FCSTD DOCUMENT  (FreeCAD 0.20R29410 (Git))
Label: prancha-editavel-A1-modelo
License: All rights reserved
objects: Sketcher::SketchObject×1
note: 1 computed .brp shape members not serialized (recipe doc carries the construction recipe); baked Part::Feature solids carry a one-line shape summary decoded from their .brp

FEATURE [Sketcher::SketchObject] Sketch
  FullyConstrained = false
  sketch-geometry (12):
    g0: LineSegment StartX=-656.822 StartY=319.687 StartZ=0 EndX=184.178 EndY=319.687 EndZ=0
    g1: LineSegment StartX=184.178 StartY=319.687 StartZ=0 EndX=184.178 EndY=-274.313 EndZ=0
    g2: LineSegment StartX=184.178 StartY=-274.313 StartZ=0 EndX=-656.822 EndY=-274.313 EndZ=0
    g3: LineSegment StartX=-656.822 StartY=-274.313 StartZ=0 EndX=-656.822 EndY=319.687 EndZ=0
    g4: LineSegment StartX=174.178 StartY=-264.313 StartZ=0 EndX=-5.8216 EndY=-264.313 EndZ=0
    g5: LineSegment StartX=-5.8216 StartY=-264.313 StartZ=0 EndX=-5.8216 EndY=-86.3544 EndZ=0
    g6: LineSegment StartX=-5.8216 StartY=-86.3544 StartZ=0 EndX=174.178 EndY=-86.3544 EndZ=0
    g7: LineSegment StartX=174.178 StartY=-86.3544 StartZ=0 EndX=174.178 EndY=-264.313 EndZ=0
    g8: LineSegment StartX=-636.822 StartY=309.687 StartZ=0 EndX=174.178 EndY=309.687 EndZ=0
    g9: LineSegment StartX=174.178 StartY=309.687 StartZ=0 EndX=174.178 EndY=-264.313 EndZ=0
    g10: LineSegment StartX=174.178 StartY=-264.313 StartZ=0 EndX=-636.822 EndY=-264.313 EndZ=0
    g11: LineSegment StartX=-636.822 StartY=-264.313 StartZ=0 EndX=-636.822 EndY=309.687 EndZ=0
  constraints (33):
    c: Coincident(g0,g1)
    c: Coincident(g1,g2)
    c: Coincident(g2,g3)
    c: Coincident(g3,g0)
    c: Horizontal(g0)
    c: Horizontal(g2)
    c: Vertical(g1)
    c: Vertical(g3)
    c: DistanceX(g0,g0) = 841
    c: DistanceY(g2,g0) = 594
    c: Coincident(g4,g5)
    c: Coincident(g5,g6)
    c: Coincident(g6,g7)
    c: Coincident(g7,g4)
    c: Horizontal(g4)
    c: Horizontal(g6)
    c: Vertical(g5)
    c: Vertical(g7)
    c: DistanceX(g5,g6) = 180
    c: DistanceY(g1,g4) = 10
    c: DistanceX(g6,g1) = 10
    c: Coincident(g8,g9)
    c: Coincident(g9,g10)
    c: Coincident(g10,g11)
    c: Coincident(g11,g8)
    c: Horizontal(g8)
    c: Horizontal(g10)
    c: Vertical(g9)
    c: Vertical(g11)
    c: DistanceX(g0,g8) = 20
    c: DistanceX(g9,g0) = 10
    c: DistanceY(g8,g0) = 10
    c: DistanceY(g2,g10) = 10
